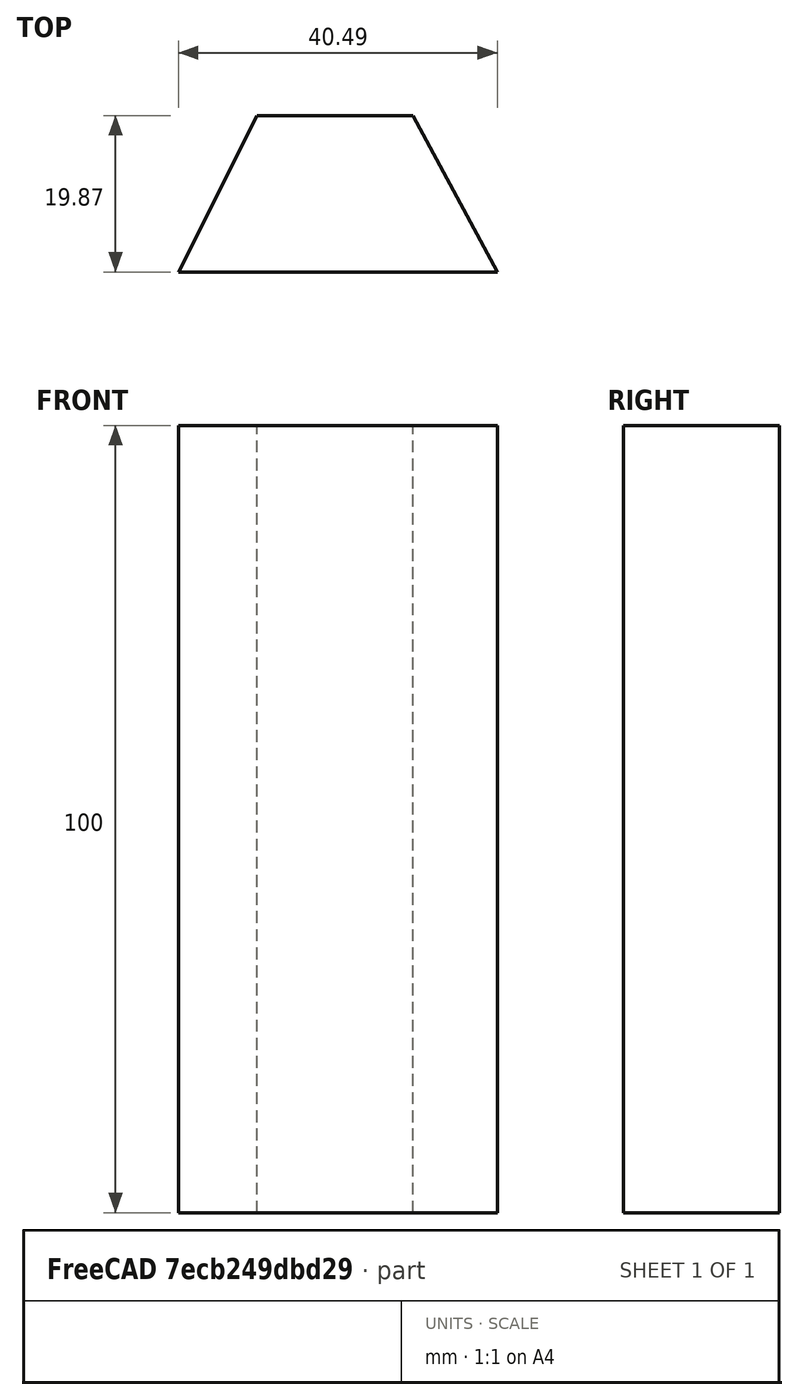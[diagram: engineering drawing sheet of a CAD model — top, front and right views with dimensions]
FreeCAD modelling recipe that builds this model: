
FCSTD DOCUMENT  (FreeCAD 1.0R39319 (Git))
Label: ojt16r01_gold.bar
License: All rights reserved
LicenseURL: https://en.wikipedia.org/wiki/All_rights_reserved
objects: Sketcher::SketchObject×1, PartDesign::Pad×1, PartDesign::Body×1
note: 6 computed .brp shape members not serialized (recipe doc carries the construction recipe); baked Part::Feature solids carry a one-line shape summary decoded from their .brp

FEATURE [Sketcher::SketchObject] Sketch
  ArcFitTolerance = 1e-06
  AttachmentSupport = -> [XY_Plane]
  FullyConstrained = false
  MakeInternals = false
  MapMode = 5
  sketch-geometry (4):
    g0: LineSegment StartX=20.7975 StartY=0 StartZ=0 EndX=10.0753 EndY=19.8683 EndZ=0
    g1: LineSegment StartX=10.0753 StartY=19.8683 StartZ=0 EndX=-9.69871 EndY=19.8683 EndZ=0
    g2: LineSegment StartX=-9.69871 StartY=19.8683 StartZ=0 EndX=-19.6922 EndY=0 EndZ=0
    g3: LineSegment StartX=-19.6922 StartY=0 StartZ=0 EndX=20.7975 EndY=0 EndZ=0
  constraints (7):
    c: PointOnObject(g2,g-1)
    c: PointOnObject(g0,g-1)
    c: Coincident(g0,g1)
    c: Horizontal(g1)
    c: Coincident(g1,g2)
    c: Coincident(g3,g2)
    c: Coincident(g3,g0)
FEATURE [PartDesign::Pad] Pad
  Direction = (0,0,1)
  Length = 100
  Length2 = 10
  Profile = -> Sketch
  ReferenceAxis = -> Sketch [N_Axis]
  Refine = true
  Suppressed = false
  Type = 0
FEATURE [PartDesign::Body] Body  label="Cos"
  AllowCompound = false
  Group = -> [Sketch,Pad]
  Origin = -> Origin
  Tip = -> Pad
